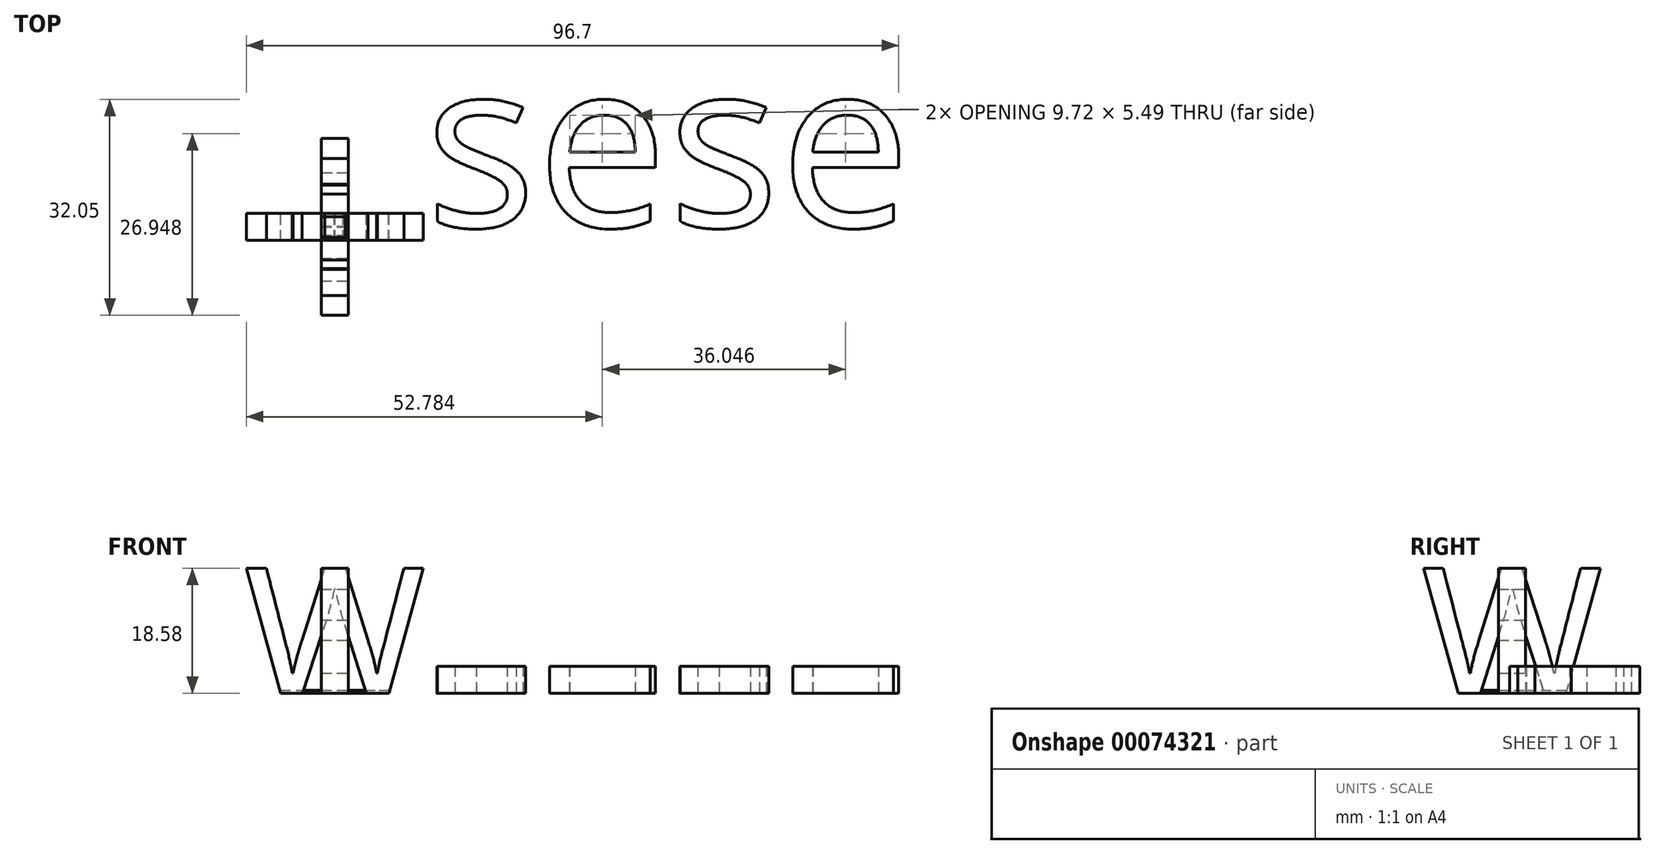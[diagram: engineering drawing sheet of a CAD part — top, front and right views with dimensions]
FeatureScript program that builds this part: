
annotation { "Feature Type Name" : "Feature", "Feature Type Description" : "" }
export const myFeature = defineFeature(function(context is Context, id is Id, definition is map)
    precondition{}
    {
        {
            var Q0;
            Q0=qCreatedBy(makeId("Front.planeOp"),FACE);
            var sketch = newSketch(context, id + "F0", { "sketchPlane" : qUnion([Q0])});
            skText(sketch, "E0", { "text": "w", "fontName": "OpenSans-Regular.ttf"});
            skLineSegment(sketch, "E1", {"start": v(0, 22.1) * mm, "end": v(0, -2) * mm, "construction": true});
            const initialGuessF0  = {"E0": [-0.0135, 0, 1, 0, 0.025]};
            skSetInitialGuess(sketch, initialGuessF0);
            skSolve(sketch);
        }
        {
            var Q0;
            Q0 = qSketchRegion(id + "F0", true);
            extrude(context, id + "F1", {"entities" : qUnion([Q0]), "depth" : 2 * mm, "hasSecondDirection" : true, "secondDirectionOppositeDirection" : true, "secondDirectionDepth" : 2 * mm});
        }
        {
            var Q0;
            Q0=qCreatedBy(makeId("Front.planeOp"),FACE);
            var sketch = newSketch(context, id + "F2", { "sketchPlane" : qUnion([Q0])});
            skLineSegment(sketch, "E2", {"start": v(0, 46.14) * mm, "end": v(0, -41.6) * mm, "construction": true});
            skSolve(sketch);
        }
        {
            var Q0;
            Q0=makeQuery(id+"F1.opExtrude","SWEPT_BODY",BODY,{"disambiguationData":[OSD([sQuery(id+"F0.wireOp",EDGE,"E0.sketch_text.stroke-0"),sQuery(id+"F0.wireOp",EDGE,"E0.sketch_text.stroke-1"),sQuery(id+"F0.wireOp",EDGE,"E0.sketch_text.stroke-2"),sQuery(id+"F0.wireOp",EDGE,"E0.sketch_text.stroke-3"),sQuery(id+"F0.wireOp",EDGE,"E0.sketch_text.stroke-4"),sQuery(id+"F0.wireOp",EDGE,"E0.sketch_text.stroke-5"),sQuery(id+"F0.wireOp",EDGE,"E0.sketch_text.stroke-6"),sQuery(id+"F0.wireOp",EDGE,"E0.sketch_text.stroke-7"),sQuery(id+"F0.wireOp",EDGE,"E0.sketch_text.stroke-8"),sQuery(id+"F0.wireOp",EDGE,"E0.sketch_text.stroke-9"),sQuery(id+"F0.wireOp",EDGE,"E0.sketch_text.stroke-10"),sQuery(id+"F0.wireOp",EDGE,"E0.sketch_text.stroke-11"),sQuery(id+"F0.wireOp",EDGE,"E0.sketch_text.stroke-12"),sQuery(id+"F0.wireOp",EDGE,"E0.sketch_text.stroke-13"),sQuery(id+"F0.wireOp",EDGE,"E0.sketch_text.stroke-14"),sQuery(id+"F0.wireOp",EDGE,"E0.sketch_text.stroke-15"),sQuery(id+"F0.wireOp",EDGE,"E0.sketch_text.stroke-16"),sQuery(id+"F0.wireOp",EDGE,"E0.sketch_text.stroke-17"),sQuery(id+"F0.wireOp",EDGE,"E0.sketch_text.stroke-18"),sQuery(id+"F0.wireOp",EDGE,"E0.sketch_text.stroke-19"),sQuery(id+"F0.wireOp",EDGE,"E0.sketch_text.stroke-20"),sQuery(id+"F0.wireOp",EDGE,"E0.sketch_text.stroke-21"),sQuery(id+"F0.wireOp",EDGE,"E0.sketch_text.stroke-22")])]});
            var Q1;
            Q1=sQuery(id+"F2.wireOp",EDGE,"E2");
            circularPattern(context, id + "F3", {"entities" : qUnion([Q0]), "axis" : qUnion([Q1]), "angle" : 90 * degree, "instanceCount" : 2});
        }
        {
            var Q0;
            Q0=qCreatedBy(makeId("Top.planeOp"),FACE);
            var sketch = newSketch(context, id + "F4", { "sketchPlane" : qUnion([Q0])});
            skText(sketch, "E3", { "text": "sese", "fontName": "OpenSans-Regular.ttf"});
            const initialGuessF4  = {"E3": [0.01332, 0, 1, 0, 0.025]};
            skSetInitialGuess(sketch, initialGuessF4);
            skSolve(sketch);
        }
        {
            var Q0;
            Q0 = qSketchRegion(id + "F4", true);
            extrude(context, id + "F5", {"entities" : qUnion([Q0]), "depth" : 4 * mm});
        }
        {
            var Q0;
            Q0=makeQuery(id+"F3.opPattern","COPY",FACE,{"derivedFrom":makeQuery(id+"F1.opExtrude","SWEPT_FACE",FACE,{"disambiguationData":[OSD([sQuery(id+"F0.wireOp",EDGE,"E0.sketch_text.stroke-22")])]}),"instanceName":"1"});
            var sketch = newSketch(context, id + "F6", { "sketchPlane" : qUnion([Q0])});
            skLineSegment(sketch, "E4.bottom", {"start": v(-8.05, 1.97) * mm, "end": v(-2, 1.97) * mm});
            skLineSegment(sketch, "E4.top", {"start": v(-8.05, -2) * mm, "end": v(-2, -2) * mm});
            skLineSegment(sketch, "E4.left", {"start": v(-8.05, 1.97) * mm, "end": v(-8.05, -2) * mm});
            skLineSegment(sketch, "E4.right", {"start": v(7.97, 1.97) * mm, "end": v(7.97, -2) * mm});
            skLineSegment(sketch, "E5.1.0", {"start": v(1.97, 8.05) * mm, "end": v(1.97, 1.97) * mm});
            skLineSegment(sketch, "E5.1.1", {"start": v(1.97, 8.05) * mm, "end": v(-2, 8.05) * mm});
            skLineSegment(sketch, "E5.1.2", {"start": v(-2, 8.05) * mm, "end": v(-2, 1.97) * mm});
            skLineSegment(sketch, "E5.1.3", {"start": v(1.97, -7.97) * mm, "end": v(-2, -7.97) * mm});
            skPoint(sketch, "E5.center", {"position": v(0, 0) * mm});
            skLineSegment(sketch, "E5.anchor1", {"start": v(0, 0) * mm, "end": v(-8.05, 1.97) * mm, "construction": true});
            skLineSegment(sketch, "E5.anchor2", {"start": v(0, 0) * mm, "end": v(1.97, 8.05) * mm, "construction": true});
            skLineSegment(sketch, "E6.trimOffspring", {"start": v(1.97, 1.97) * mm, "end": v(7.97, 1.97) * mm});
            skLineSegment(sketch, "E7.trimOffspring", {"start": v(-2, -2) * mm, "end": v(-2, -7.97) * mm});
            skLineSegment(sketch, "E8.trimOffspring", {"start": v(1.97, -2) * mm, "end": v(7.97, -2) * mm});
            skLineSegment(sketch, "E9.trimOffspring", {"start": v(1.97, -2) * mm, "end": v(1.97, -7.97) * mm});
            skSolve(sketch);
        }
        {
            var Q0;
            {var subQ2=sQuery(id+"F6.wireOp",EDGE,"E4.bottom");Q0=makeQuery(id+"F6.imprint","IMPRINT",FACE,{"disambiguationData":[TD([[makeQuery(id+"F6.imprint","IMPRINT",EDGE,{"derivedFrom":subQ2}),-1.0]])]});}
            extrude(context, id + "F7", {"entities" : qUnion([Q0]), "oppositeDirection" : true, "depth" : .5 * mm});
        }
    });
